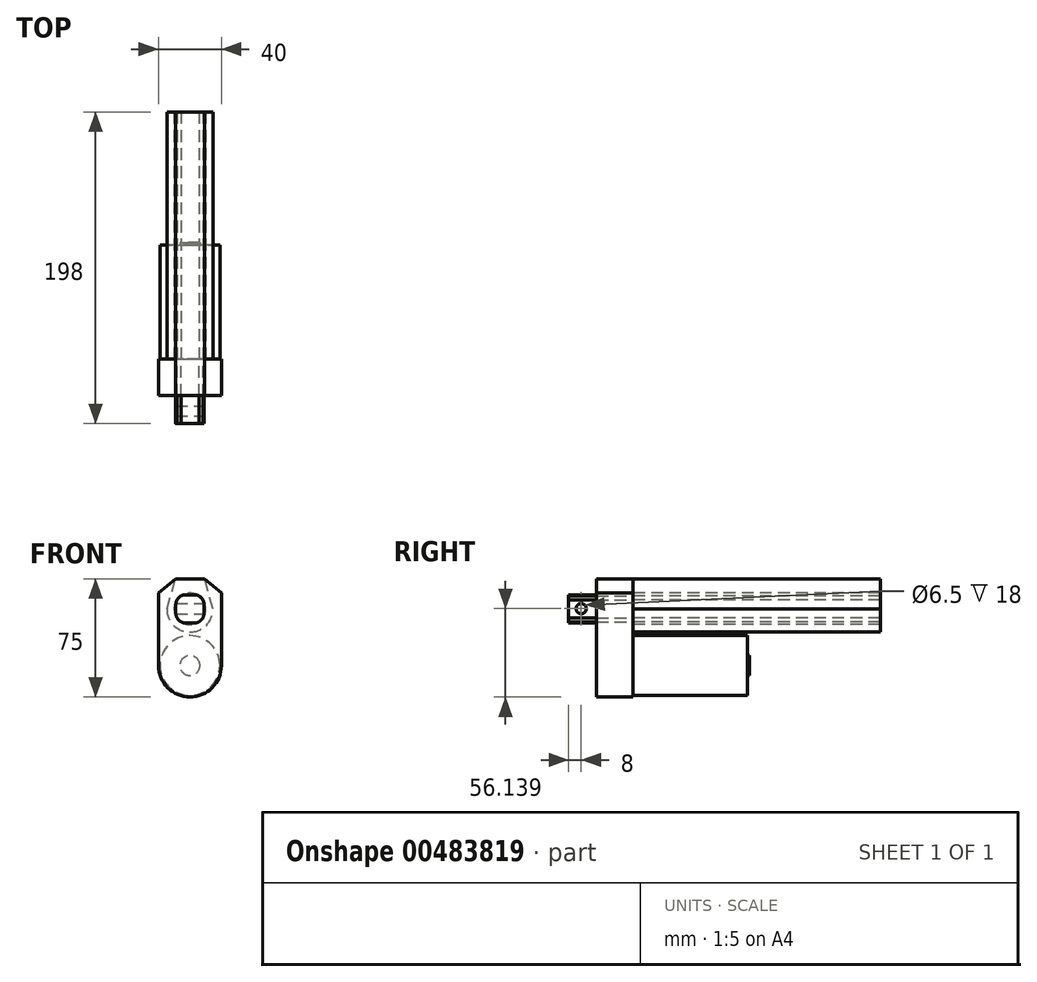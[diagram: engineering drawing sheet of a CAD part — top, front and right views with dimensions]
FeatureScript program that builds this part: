
annotation { "Feature Type Name" : "Feature", "Feature Type Description" : "" }
export const myFeature = defineFeature(function(context is Context, id is Id, definition is map)
    precondition{}
    {
        {
            var Q0;
            Q0=qCreatedBy(makeId("Front.planeOp"),FACE);
            var sketch = newSketch(context, id + "F0", { "sketchPlane" : qUnion([Q0])});
            skLineSegment(sketch, "E0.bottom", {"start": v(-20, 23.02) * mm, "end": v(20, 23.02) * mm});
            skLineSegment(sketch, "E0.top", {"start": v(-20, -23.02) * mm, "end": v(20, -23.02) * mm});
            skLineSegment(sketch, "E0.left", {"start": v(-20, 23.02) * mm, "end": v(-20, -23.02) * mm});
            skLineSegment(sketch, "E0.right", {"start": v(20, 23.02) * mm, "end": v(20, -23.02) * mm});
            skPoint(sketch, "E0.middle", {"position": v(0, 0) * mm});
            skArc(sketch, "E1", {"start": v(-20, -23.02) * mm, "mid": v(0, -43.02) * mm, "end": v(20, -23.02) * mm});
            skLineSegment(sketch, "E2", {"start": v(20, 23.02) * mm, "end": v(9.25, 31.98) * mm});
            skLineSegment(sketch, "E3", {"start": v(9.25, 31.98) * mm, "end": v(-9.25, 31.98) * mm});
            skLineSegment(sketch, "E4", {"start": v(-9.25, 31.98) * mm, "end": v(-20, 23.02) * mm});
            skLineSegment(sketch, "E5.bottom", {"start": v(-2.65, 21.98) * mm, "end": v(2.65, 21.98) * mm});
            skLineSegment(sketch, "E5.top", {"start": v(-2.65, 3.98) * mm, "end": v(2.65, 3.98) * mm});
            skLineSegment(sketch, "E5.left", {"start": v(-9, 15.63) * mm, "end": v(-9, 10.33) * mm});
            skLineSegment(sketch, "E5.right", {"start": v(9, 15.63) * mm, "end": v(9, 10.33) * mm});
            skPoint(sketch, "E5.middle", {"position": v(0, 12.98) * mm});
            skPoint(sketch, "E6.visualSharp", {"position": v(9, 21.98) * mm});
            skArc(sketch, "E6.filletArc", {"start": v(9, 15.63) * mm, "mid": v(7.14, 20.12) * mm, "end": v(2.65, 21.98) * mm});
            skPoint(sketch, "E7.visualSharp", {"position": v(-9, 21.98) * mm});
            skArc(sketch, "E7.filletArc", {"start": v(-2.65, 21.98) * mm, "mid": v(-7.14, 20.12) * mm, "end": v(-9, 15.63) * mm});
            skPoint(sketch, "E8.visualSharp", {"position": v(-9, 3.98) * mm});
            skArc(sketch, "E8.filletArc", {"start": v(-9, 10.33) * mm, "mid": v(-7.14, 5.84) * mm, "end": v(-2.65, 3.98) * mm});
            skPoint(sketch, "E9.visualSharp", {"position": v(9, 3.98) * mm});
            skArc(sketch, "E9.filletArc", {"start": v(2.65, 3.98) * mm, "mid": v(7.14, 5.84) * mm, "end": v(9, 10.33) * mm});
            skCircle(sketch, "E10", {"center": v(0, -23.02) * mm, "radius": 19 * mm});
            skCircle(sketch, "E11", {"center": v(0, 12.98) * mm, "radius": 10 * mm});
            skLineSegment(sketch, "E12", {"start": v(0, 12.98) * mm, "end": v(-14.65, 12.98) * mm});
            skLineSegment(sketch, "E13", {"start": v(-14.65, 12.98) * mm, "end": v(0, 12.98) * mm});
            skLineSegment(sketch, "E14", {"start": v(0, 12.98) * mm, "end": v(14.65, 12.98) * mm});
            skPoint(sketch, "E14.endSnap0", {"position": v(9, 12.98) * mm});
            skLineSegment(sketch, "E15", {"start": v(14.65, 12.98) * mm, "end": v(9.25, 31.98) * mm});
            skLineSegment(sketch, "E16", {"start": v(-14.65, 12.98) * mm, "end": v(-9.25, 31.98) * mm});
            skArc(sketch, "E17", {"start": v(-14.65, 12.98) * mm, "mid": v(0, -1.76) * mm, "end": v(14.65, 12.98) * mm});
            skCircle(sketch, "E18", {"center": v(0, -23.02) * mm, "radius": 6.38 * mm});
            skSolve(sketch);
        }
        {
            var Q0;
            Q0=qCreatedBy(makeId("Right.planeOp"),FACE);
            var sketch = newSketch(context, id + "F1", { "sketchPlane" : qUnion([Q0])});
            skCircle(sketch, "E19", {"center": v(-33, 13.12) * mm, "radius": 3.25 * mm});
            skSolve(sketch);
        }
        {
            var Q0;
            Q0 = qSketchRegion(id + "F0", true);
            var Q1;
            {var subQ9=sQuery(id+"F0.wireOp",EDGE,"E17");Q1=makeQuery(id+"F0.imprint","IMPRINT",FACE,{"disambiguationData":[TD([[makeQuery(id+"F0.imprint","IMPRINT",EDGE,{"derivedFrom":subQ9}),1.0]])]});}
            var Q2;
            {var subQ5=sQuery(id+"F0.wireOp",EDGE,"E16");var subQ6=sQuery(id+"F0.wireOp",EDGE,"E0.bottom");var subQ7=makeQuery(id+"F0.imprint","INTERSECT",VERTEX,{"derivedFrom":[subQ6,subQ5]});Q2=makeQuery(id+"F0.imprint","IMPRINT",FACE,{"disambiguationData":[TD([[makeQuery(id+"F0.imprint","IMPRINT",EDGE,{"disambiguationData":[TD([[subQ7,-1.0]])],"derivedFrom":subQ6}),-1.0]])]});}
            var Q3;
            {var subQ0=sQuery(id+"F0.wireOp",EDGE,"E5.bottom");Q3=makeQuery(id+"F0.imprint","IMPRINT",FACE,{"disambiguationData":[TD([[makeQuery(id+"F0.imprint","IMPRINT",EDGE,{"derivedFrom":subQ0}),1.0]])]});}
            var Q4;
            {var subQ0=sQuery(id+"F0.wireOp",EDGE,"E7.filletArc");var subQ1=sQuery(id+"F0.wireOp",EDGE,"E5.left");var subQ2=makeQuery(id+"F0.imprint","INTERSECT",VERTEX,{"derivedFrom":[subQ1,subQ0]});Q4=makeQuery(id+"F0.imprint","IMPRINT",FACE,{"disambiguationData":[TD([[makeQuery(id+"F0.imprint","IMPRINT",EDGE,{"disambiguationData":[TD([[subQ2,-1.0]])],"derivedFrom":subQ1}),-1.0]])]});}
            var Q5;
            {var subQ0=sQuery(id+"F0.wireOp",EDGE,"E8.filletArc");var subQ1=sQuery(id+"F0.wireOp",EDGE,"E5.left");var subQ2=makeQuery(id+"F0.imprint","INTERSECT",VERTEX,{"derivedFrom":[subQ1,subQ0]});Q5=makeQuery(id+"F0.imprint","IMPRINT",FACE,{"disambiguationData":[TD([[makeQuery(id+"F0.imprint","IMPRINT",EDGE,{"disambiguationData":[TD([[subQ2,1.0]])],"derivedFrom":subQ1}),-1.0]])]});}
            var Q6;
            {var subQ0=sQuery(id+"F0.wireOp",EDGE,"E9.filletArc");var subQ1=sQuery(id+"F0.wireOp",EDGE,"E5.right");var subQ2=makeQuery(id+"F0.imprint","INTERSECT",VERTEX,{"derivedFrom":[subQ1,subQ0]});Q6=makeQuery(id+"F0.imprint","IMPRINT",FACE,{"disambiguationData":[TD([[makeQuery(id+"F0.imprint","IMPRINT",EDGE,{"disambiguationData":[TD([[subQ2,1.0]])],"derivedFrom":subQ1}),1.0]])]});}
            var Q7;
            {var subQ0=sQuery(id+"F0.wireOp",EDGE,"E6.filletArc");var subQ1=sQuery(id+"F0.wireOp",EDGE,"E5.right");var subQ2=makeQuery(id+"F0.imprint","INTERSECT",VERTEX,{"derivedFrom":[subQ1,subQ0]});Q7=makeQuery(id+"F0.imprint","IMPRINT",FACE,{"disambiguationData":[TD([[makeQuery(id+"F0.imprint","IMPRINT",EDGE,{"disambiguationData":[TD([[subQ2,-1.0]])],"derivedFrom":subQ1}),1.0]])]});}
            var Q8;
            {var subQ0=sQuery(id+"F0.wireOp",EDGE,"E5.top");Q8=makeQuery(id+"F0.imprint","IMPRINT",FACE,{"disambiguationData":[TD([[makeQuery(id+"F0.imprint","IMPRINT",EDGE,{"derivedFrom":subQ0}),-1.0]])]});}
            var Q9;
            {var subQ0=sQuery(id+"F0.wireOp",EDGE,"E10");var subQ1=sQuery(id+"F0.wireOp",EDGE,"E0.top");var subQ2=makeQuery(id+"F0.imprint","INTERSECT",VERTEX,{"disambiguationData":[OD(0.0)],"derivedFrom":[subQ1,subQ0]});Q9=makeQuery(id+"F0.imprint","IMPRINT",FACE,{"disambiguationData":[TD([[makeQuery(id+"F0.imprint","IMPRINT",EDGE,{"disambiguationData":[TD([[subQ2,-1.0]])],"derivedFrom":subQ1}),1.0]])]});}
            var Q10;
            {var subQ0=sQuery(id+"F0.wireOp",EDGE,"E18");var subQ1=sQuery(id+"F0.wireOp",EDGE,"E0.top");var subQ2=makeQuery(id+"F0.imprint","INTERSECT",VERTEX,{"disambiguationData":[OD(0.0)],"derivedFrom":[subQ1,subQ0]});Q10=makeQuery(id+"F0.imprint","IMPRINT",FACE,{"disambiguationData":[TD([[makeQuery(id+"F0.imprint","IMPRINT",EDGE,{"disambiguationData":[TD([[subQ2,-1.0]])],"derivedFrom":subQ1}),1.0]])]});}
            var Q11;
            {var subQ0=sQuery(id+"F0.wireOp",EDGE,"E18");var subQ1=sQuery(id+"F0.wireOp",EDGE,"E0.top");var subQ2=makeQuery(id+"F0.imprint","INTERSECT",VERTEX,{"disambiguationData":[OD(0.0)],"derivedFrom":[subQ1,subQ0]});Q11=makeQuery(id+"F0.imprint","IMPRINT",FACE,{"disambiguationData":[TD([[makeQuery(id+"F0.imprint","IMPRINT",EDGE,{"disambiguationData":[TD([[subQ2,-1.0]])],"derivedFrom":subQ1}),-1.0]])]});}
            var Q12;
            {var subQ0=sQuery(id+"F0.wireOp",EDGE,"E10");var subQ1=sQuery(id+"F0.wireOp",EDGE,"E0.top");var subQ2=makeQuery(id+"F0.imprint","INTERSECT",VERTEX,{"disambiguationData":[OD(0.0)],"derivedFrom":[subQ1,subQ0]});Q12=makeQuery(id+"F0.imprint","IMPRINT",FACE,{"disambiguationData":[TD([[makeQuery(id+"F0.imprint","IMPRINT",EDGE,{"disambiguationData":[TD([[subQ2,-1.0]])],"derivedFrom":subQ1}),-1.0]])]});}
            extrude(context, id + "F2", {"entities" : qUnion([Q0, Q1, Q2, Q3, Q4, Q5, Q6, Q7, Q8, Q9, Q10, Q11, Q12]), "depth" : 23.25 * mm});
        }
        {
            var Q0;
            {var subQ4=sQuery(id+"F0.wireOp",EDGE,"E5.bottom");Q0=makeQuery(id+"F0.imprint","IMPRINT",FACE,{"disambiguationData":[TD([[makeQuery(id+"F0.imprint","IMPRINT",EDGE,{"derivedFrom":subQ4}),-1.0]])]});}
            var Q1;
            {var subQ16=sQuery(id+"F0.wireOp",EDGE,"E5.top");Q1=makeQuery(id+"F0.imprint","IMPRINT",FACE,{"disambiguationData":[TD([[makeQuery(id+"F0.imprint","IMPRINT",EDGE,{"derivedFrom":subQ16}),1.0]])]});}
            extrude(context, id + "F3", {"entities" : qUnion([Q0, Q1]), "operationType" : NewBodyOperationType.ADD, "depth" : 41 * mm});
        }
        {
            var Q0;
            {var subQ0=sQuery(id+"F0.wireOp",EDGE,"E10");var subQ1=sQuery(id+"F0.wireOp",EDGE,"E0.top");var subQ2=makeQuery(id+"F0.imprint","INTERSECT",VERTEX,{"disambiguationData":[OD(0.0)],"derivedFrom":[subQ1,subQ0]});Q0=makeQuery(id+"F0.imprint","IMPRINT",FACE,{"disambiguationData":[TD([[makeQuery(id+"F0.imprint","IMPRINT",EDGE,{"disambiguationData":[TD([[subQ2,-1.0]])],"derivedFrom":subQ1}),1.0]])]});}
            var Q1;
            {var subQ0=sQuery(id+"F0.wireOp",EDGE,"E10");var subQ1=sQuery(id+"F0.wireOp",EDGE,"E0.top");var subQ2=makeQuery(id+"F0.imprint","INTERSECT",VERTEX,{"disambiguationData":[OD(0.0)],"derivedFrom":[subQ1,subQ0]});Q1=makeQuery(id+"F0.imprint","IMPRINT",FACE,{"disambiguationData":[TD([[makeQuery(id+"F0.imprint","IMPRINT",EDGE,{"disambiguationData":[TD([[subQ2,-1.0]])],"derivedFrom":subQ1}),-1.0]])]});}
            extrude(context, id + "F4", {"entities" : qUnion([Q0, Q1]), "operationType" : NewBodyOperationType.ADD, "oppositeDirection" : true, "depth" : 72.5 * mm});
        }
        {
            var Q0;
            {var subQ0=sQuery(id+"F0.wireOp",EDGE,"E18");var subQ1=sQuery(id+"F0.wireOp",EDGE,"E0.top");var subQ2=makeQuery(id+"F0.imprint","INTERSECT",VERTEX,{"disambiguationData":[OD(0.0)],"derivedFrom":[subQ1,subQ0]});Q0=makeQuery(id+"F0.imprint","IMPRINT",FACE,{"disambiguationData":[TD([[makeQuery(id+"F0.imprint","IMPRINT",EDGE,{"disambiguationData":[TD([[subQ2,-1.0]])],"derivedFrom":subQ1}),1.0]])]});}
            var Q1;
            {var subQ0=sQuery(id+"F0.wireOp",EDGE,"E18");var subQ1=sQuery(id+"F0.wireOp",EDGE,"E0.top");var subQ2=makeQuery(id+"F0.imprint","INTERSECT",VERTEX,{"disambiguationData":[OD(0.0)],"derivedFrom":[subQ1,subQ0]});Q1=makeQuery(id+"F0.imprint","IMPRINT",FACE,{"disambiguationData":[TD([[makeQuery(id+"F0.imprint","IMPRINT",EDGE,{"disambiguationData":[TD([[subQ2,-1.0]])],"derivedFrom":subQ1}),-1.0]])]});}
            extrude(context, id + "F5", {"entities" : qUnion([Q0, Q1]), "operationType" : NewBodyOperationType.ADD, "oppositeDirection" : true, "depth" : 74 * mm});
        }
        {
            var Q0;
            {var subQ5=sQuery(id+"F0.wireOp",EDGE,"E3");Q0=makeQuery(id+"F0.imprint","IMPRINT",FACE,{"disambiguationData":[TD([[makeQuery(id+"F0.imprint","IMPRINT",EDGE,{"derivedFrom":subQ5}),1.0]])]});}
            var Q1;
            {var subQ5=sQuery(id+"F0.wireOp",EDGE,"E16");var subQ6=sQuery(id+"F0.wireOp",EDGE,"E0.bottom");var subQ7=makeQuery(id+"F0.imprint","INTERSECT",VERTEX,{"derivedFrom":[subQ6,subQ5]});Q1=makeQuery(id+"F0.imprint","IMPRINT",FACE,{"disambiguationData":[TD([[makeQuery(id+"F0.imprint","IMPRINT",EDGE,{"disambiguationData":[TD([[subQ7,-1.0]])],"derivedFrom":subQ6}),-1.0]])]});}
            var Q2;
            {var subQ9=sQuery(id+"F0.wireOp",EDGE,"E17");Q2=makeQuery(id+"F0.imprint","IMPRINT",FACE,{"disambiguationData":[TD([[makeQuery(id+"F0.imprint","IMPRINT",EDGE,{"derivedFrom":subQ9}),1.0]])]});}
            extrude(context, id + "F6", {"entities" : qUnion([Q0, Q1, Q2]), "operationType" : NewBodyOperationType.ADD, "oppositeDirection" : true, "depth" : 157 * mm});
        }
        {
            var Q0;
            Q0=sQuery(id+"F1.wireOp",VERTEX,"E19.center");
            var Q1;
            Q1=makeQuery(id+"F2.opExtrude","SWEPT_BODY",BODY,{"disambiguationData":[OSD([sQuery(id+"F0.wireOp",EDGE,"E0.left"),sQuery(id+"F0.wireOp",EDGE,"E0.right"),sQuery(id+"F0.wireOp",EDGE,"E1"),sQuery(id+"F0.wireOp",EDGE,"E2"),sQuery(id+"F0.wireOp",EDGE,"E3"),sQuery(id+"F0.wireOp",EDGE,"E4"),sQuery(id+"F0.wireOp",EDGE,"E5.bottom"),sQuery(id+"F0.wireOp",EDGE,"E5.top"),sQuery(id+"F0.wireOp",EDGE,"E5.left"),sQuery(id+"F0.wireOp",EDGE,"E5.right"),sQuery(id+"F0.wireOp",EDGE,"E6.filletArc"),sQuery(id+"F0.wireOp",EDGE,"E7.filletArc"),sQuery(id+"F0.wireOp",EDGE,"E8.filletArc"),sQuery(id+"F0.wireOp",EDGE,"E9.filletArc")])]});
            hole(context, id + "F7", {"style" : HoleStyle.SIMPLE, "endStyle" : HoleEndStyle.THROUGH, "holeDiameter" : 6.5 * mm, "isTappedThrough" : true, "tappedDepth" : 12.7 * mm, "tapClearance" : 3, "locations" : qUnion([Q0]), "scope" : qUnion([Q1])});
        }
        {
            var Q0;
            Q0=sQuery(id+"F1.wireOp",VERTEX,"E19.center");
            var Q1;
            Q1=makeQuery(id+"F2.opExtrude","SWEPT_BODY",BODY,{"disambiguationData":[OSD([sQuery(id+"F0.wireOp",EDGE,"E0.left"),sQuery(id+"F0.wireOp",EDGE,"E0.right"),sQuery(id+"F0.wireOp",EDGE,"E1"),sQuery(id+"F0.wireOp",EDGE,"E2"),sQuery(id+"F0.wireOp",EDGE,"E3"),sQuery(id+"F0.wireOp",EDGE,"E4"),sQuery(id+"F0.wireOp",EDGE,"E5.bottom"),sQuery(id+"F0.wireOp",EDGE,"E5.top"),sQuery(id+"F0.wireOp",EDGE,"E5.left"),sQuery(id+"F0.wireOp",EDGE,"E5.right"),sQuery(id+"F0.wireOp",EDGE,"E6.filletArc"),sQuery(id+"F0.wireOp",EDGE,"E7.filletArc"),sQuery(id+"F0.wireOp",EDGE,"E8.filletArc"),sQuery(id+"F0.wireOp",EDGE,"E9.filletArc")])]});
            hole(context, id + "F8", {"style" : HoleStyle.SIMPLE, "endStyle" : HoleEndStyle.THROUGH, "oppositeDirection" : true, "holeDiameter" : 6.5 * mm, "isTappedThrough" : true, "tappedDepth" : 12.7 * mm, "tapClearance" : 3, "locations" : qUnion([Q0]), "scope" : qUnion([Q1])});
        }
    });
